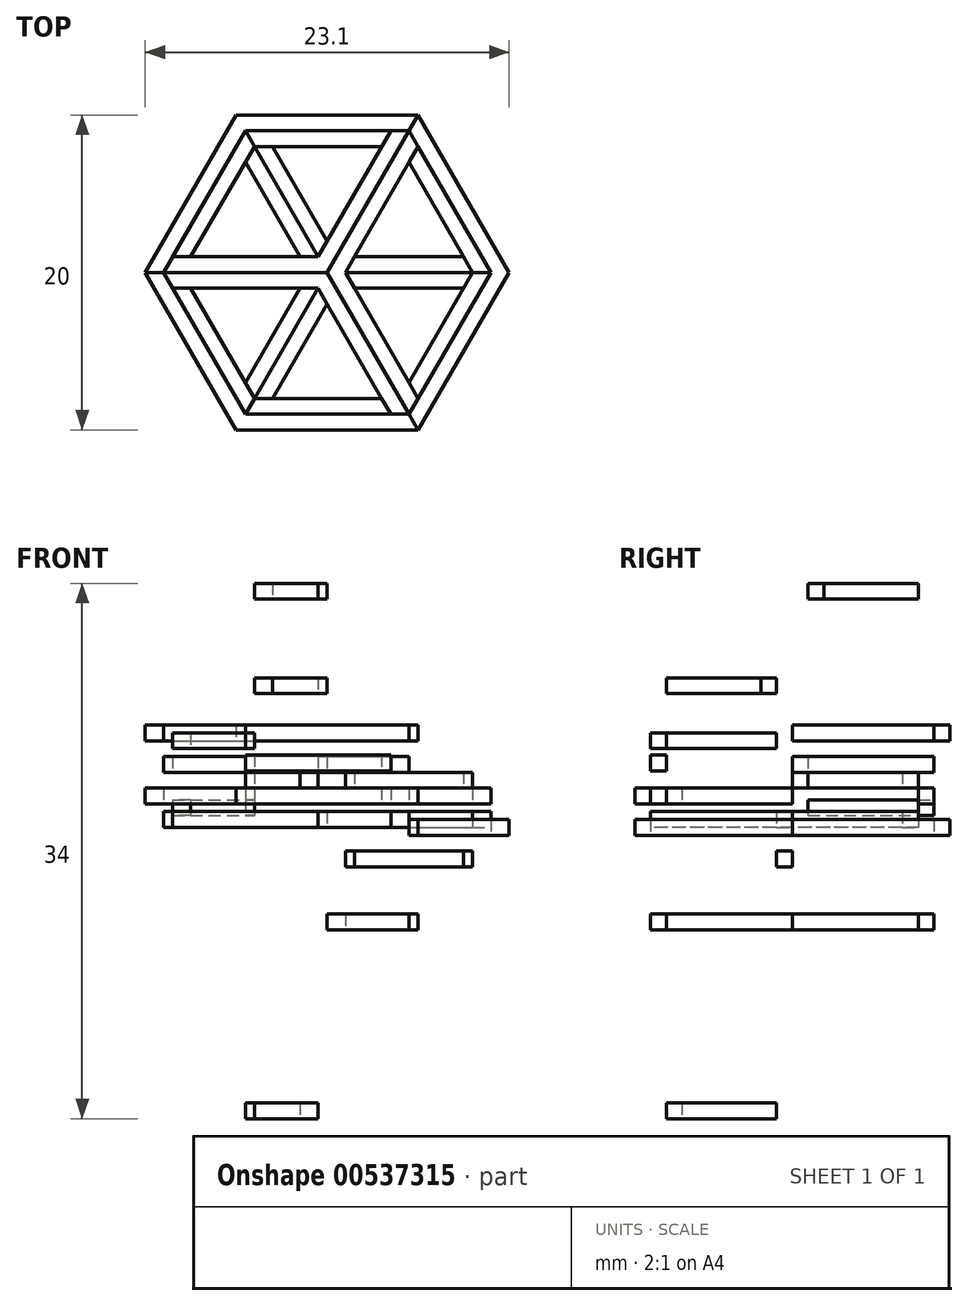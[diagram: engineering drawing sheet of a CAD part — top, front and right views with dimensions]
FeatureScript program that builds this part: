
annotation { "Feature Type Name" : "Feature", "Feature Type Description" : "" }
export const myFeature = defineFeature(function(context is Context, id is Id, definition is map)
    precondition{}
    {
        {
            var Q0;
            Q0=qCreatedBy(makeId("Top.planeOp"),FACE);
            var sketch = newSketch(context, id + "F0", { "sketchPlane" : qUnion([Q0])});
            skLineSegment(sketch, "E0", {"start": v(0, 0) * mm, "end": v(0, 10) * mm});
            skArc(sketch, "E1.cCircle", {"start": v(4.36, 9) * mm, "mid": v(-5, -8.66) * mm, "end": v(5.61, 8.27) * mm, "construction": true});
            skLineSegment(sketch, "E1.0", {"start": v(-5.77, 10) * mm, "end": v(5.77, 10) * mm});
            skLineSegment(sketch, "E1.1", {"start": v(5.77, 10) * mm, "end": v(11.55, 0) * mm});
            skLineSegment(sketch, "E1.2", {"start": v(11.55, 0) * mm, "end": v(5.77, -10) * mm});
            skLineSegment(sketch, "E1.3", {"start": v(5.77, -10) * mm, "end": v(-5.77, -10) * mm});
            skLineSegment(sketch, "E1.4", {"start": v(-5.77, -10) * mm, "end": v(-11.55, 0) * mm});
            skLineSegment(sketch, "E1.5", {"start": v(-11.55, 0) * mm, "end": v(-5.77, 10) * mm});
            skPoint(sketch, "E1.0.midPoint", {"position": v(0, 10) * mm});
            skLineSegment(sketch, "E2.0", {"start": v(-10.4, 0) * mm, "end": v(-5.2, 9) * mm});
            skLineSegment(sketch, "E2.1", {"start": v(5.2, 9) * mm, "end": v(10.4, 0) * mm});
            skLineSegment(sketch, "E2.2", {"start": v(10.4, 0) * mm, "end": v(5.2, -9) * mm});
            skLineSegment(sketch, "E2.3", {"start": v(-5.2, 9) * mm, "end": v(5.2, 9) * mm});
            skLineSegment(sketch, "E2.4", {"start": v(5.2, -9) * mm, "end": v(-5.2, -9) * mm});
            skLineSegment(sketch, "E2.5", {"start": v(-5.2, -9) * mm, "end": v(-10.4, 0) * mm});
            skLineSegment(sketch, "E3.0", {"start": v(-9.24, 0) * mm, "end": v(-4.62, 8) * mm});
            skLineSegment(sketch, "E3.1", {"start": v(4.62, 8) * mm, "end": v(9.24, 0) * mm});
            skLineSegment(sketch, "E3.2", {"start": v(9.24, 0) * mm, "end": v(4.62, -8) * mm});
            skLineSegment(sketch, "E3.3", {"start": v(-4.62, 8) * mm, "end": v(4.62, 8) * mm});
            skLineSegment(sketch, "E3.4", {"start": v(4.62, -8) * mm, "end": v(-4.62, -8) * mm});
            skLineSegment(sketch, "E3.5", {"start": v(-4.62, -8) * mm, "end": v(-9.24, 0) * mm});
            skLineSegment(sketch, "E4", {"start": v(0, 0) * mm, "end": v(4.62, -8) * mm});
            skLineSegment(sketch, "E5", {"start": v(0, 0) * mm, "end": v(4.62, 8) * mm});
            skLineSegment(sketch, "E6", {"start": v(0, 0) * mm, "end": v(-9.24, 0) * mm});
            skLineSegment(sketch, "E7.0", {"start": v(-0.58, 1) * mm, "end": v(3.46, 8) * mm});
            skLineSegment(sketch, "E7.1", {"start": v(-0.58, 1) * mm, "end": v(-9.81, 1) * mm});
            skLineSegment(sketch, "E8.0", {"start": v(1.15, 0) * mm, "end": v(5.77, 8) * mm});
            skLineSegment(sketch, "E9.0", {"start": v(-0.58, -1) * mm, "end": v(4.04, -9) * mm});
            skLineSegment(sketch, "E10.0", {"start": v(1.15, 0) * mm, "end": v(5.77, -8) * mm});
            skLineSegment(sketch, "E11.0", {"start": v(-0.58, -1) * mm, "end": v(-9.81, -1) * mm});
            skLineSegment(sketch, "E12.1.0", {"start": v(0.58, -1) * mm, "end": v(-3.46, -8) * mm});
            skLineSegment(sketch, "E12.1.1", {"start": v(-1.15, 0) * mm, "end": v(-5.2, -7) * mm});
            skLineSegment(sketch, "E12.1.2", {"start": v(-1.15, 0) * mm, "end": v(-5.2, 7) * mm});
            skLineSegment(sketch, "E12.1.3", {"start": v(0.58, 1) * mm, "end": v(-3.46, 8) * mm});
            skLineSegment(sketch, "E12.1.4", {"start": v(0, 0) * mm, "end": v(-4.62, 8) * mm});
            skLineSegment(sketch, "E12.1.5", {"start": v(0.58, 1) * mm, "end": v(8.66, 1) * mm});
            skLineSegment(sketch, "E12.1.6", {"start": v(0.58, -1) * mm, "end": v(8.66, -1) * mm});
            skLineSegment(sketch, "E12.1.7", {"start": v(0, 0) * mm, "end": v(9.24, 0) * mm});
            skLineSegment(sketch, "E12.1.8", {"start": v(0, 0) * mm, "end": v(-4.62, -8) * mm});
            skLineSegment(sketch, "E13", {"start": v(-4.62, 8) * mm, "end": v(-5.2, 9) * mm});
            skLineSegment(sketch, "E14", {"start": v(3.46, 8) * mm, "end": v(4.04, 9) * mm});
            skPoint(sketch, "E15.orphan", {"position": v(5.2, 7) * mm});
            skPoint(sketch, "E16.orphan", {"position": v(5.2, -7) * mm});
            skPoint(sketch, "E17.orphan", {"position": v(3.46, -8) * mm});
            skPoint(sketch, "E18.orphan", {"position": v(-8.66, -1) * mm});
            skPoint(sketch, "E19.orphan", {"position": v(-8.66, 1) * mm});
            skLineSegment(sketch, "E20", {"start": v(5.2, 9) * mm, "end": v(5.77, 10) * mm});
            skLineSegment(sketch, "E21", {"start": v(-10.4, 0) * mm, "end": v(-11.55, 0) * mm});
            skLineSegment(sketch, "E22", {"start": v(5.2, -9) * mm, "end": v(5.77, -10) * mm});
            skLineSegment(sketch, "E23", {"start": v(9.24, 0) * mm, "end": v(10.4, 0) * mm});
            skLineSegment(sketch, "E24", {"start": v(-4.62, -8) * mm, "end": v(-5.2, -9) * mm});
            skLineSegment(sketch, "E25", {"start": v(4.62, 8) * mm, "end": v(5.2, 9) * mm});
            skLineSegment(sketch, "E26", {"start": v(-9.24, 0) * mm, "end": v(-10.4, 0) * mm});
            skLineSegment(sketch, "E27", {"start": v(4.62, -8) * mm, "end": v(5.2, -9) * mm});
            skSolve(sketch);
        }
        {
            var Q0;
            {var subQ3=sQuery(id+"F0.wireOp",EDGE,"E1.5");Q0=makeQuery(id+"F0.imprint","IMPRINT",FACE,{"disambiguationData":[TD([[makeQuery(id+"F0.imprint","IMPRINT",EDGE,{"derivedFrom":subQ3}),-1.0]])]});}
            var Q1;
            {var subQ0=sQuery(id+"F0.wireOp",EDGE,"E20");Q1=makeQuery(id+"F0.imprint","IMPRINT",FACE,{"disambiguationData":[TD([[makeQuery(id+"F0.imprint","IMPRINT",EDGE,{"derivedFrom":subQ0}),1.0]])]});}
            extrude(context, id + "F1", {"entities" : qUnion([Q0, Q1]), "depth" : 1 * mm, "offsetDistance" : 25 * mm});
        }
        {
            var Q0;
            {var subQ1=sQuery(id+"F0.wireOp",EDGE,"E3.0");var subQ3=sQuery(id+"F0.wireOp",EDGE,"E7.1");var subQ4=makeQuery(id+"F0.imprint","INTERSECT",VERTEX,{"derivedFrom":[subQ1,subQ3]});Q0=makeQuery(id+"F0.imprint","IMPRINT",FACE,{"disambiguationData":[TD([[makeQuery(id+"F0.imprint","IMPRINT",EDGE,{"disambiguationData":[TD([[subQ4,1.0]])],"derivedFrom":subQ3}),1.0]])]});}
            var Q1;
            {var subQ3=sQuery(id+"F0.wireOp",EDGE,"E12.1.2");var subQ5=sQuery(id+"F0.wireOp",EDGE,"E7.1");var subQ7=makeQuery(id+"F0.imprint","INTERSECT",VERTEX,{"derivedFrom":[subQ5,subQ3]});Q1=makeQuery(id+"F0.imprint","IMPRINT",FACE,{"disambiguationData":[TD([[makeQuery(id+"F0.imprint","IMPRINT",EDGE,{"disambiguationData":[TD([[subQ7,1.0]])],"derivedFrom":subQ5}),1.0]])]});}
            var Q2;
            {var subQ0=sQuery(id+"F0.wireOp",EDGE,"E12.1.4");var subQ3=sQuery(id+"F0.wireOp",EDGE,"E7.0");var subQ5=makeQuery(id+"F0.imprint","INTERSECT",VERTEX,{"derivedFrom":[subQ3,sQuery(id+"F0.wireOp",EDGE,"E7.1"),subQ0]});Q2=makeQuery(id+"F0.imprint","IMPRINT",FACE,{"disambiguationData":[TD([[makeQuery(id+"F0.imprint","IMPRINT",EDGE,{"disambiguationData":[TD([[subQ5,-1.0]])],"derivedFrom":subQ3}),-1.0]])]});}
            var Q3;
            {var subQ0=sQuery(id+"F0.wireOp",EDGE,"E5");var subQ3=sQuery(id+"F0.wireOp",EDGE,"E12.1.3");var subQ5=makeQuery(id+"F0.imprint","INTERSECT",VERTEX,{"derivedFrom":[subQ0,subQ3,sQuery(id+"F0.wireOp",EDGE,"E12.1.5")]});Q3=makeQuery(id+"F0.imprint","IMPRINT",FACE,{"disambiguationData":[TD([[makeQuery(id+"F0.imprint","IMPRINT",EDGE,{"disambiguationData":[TD([[subQ5,-1.0]])],"derivedFrom":subQ3}),1.0]])]});}
            var Q4;
            {var subQ0=sQuery(id+"F0.wireOp",EDGE,"E5");var subQ1=sQuery(id+"F0.wireOp",EDGE,"E3.3");var subQ2=makeQuery(id+"F0.imprint","INTERSECT",VERTEX,{"derivedFrom":[sQuery(id+"F0.wireOp",EDGE,"E3.1"),subQ1,subQ0]});Q4=makeQuery(id+"F0.imprint","IMPRINT",FACE,{"disambiguationData":[TD([[makeQuery(id+"F0.imprint","IMPRINT",EDGE,{"disambiguationData":[TD([[subQ2,1.0]])],"derivedFrom":subQ1}),-1.0]])]});}
            var Q5;
            {var subQ0=sQuery(id+"F0.wireOp",EDGE,"E26");Q5=makeQuery(id+"F0.imprint","IMPRINT",FACE,{"disambiguationData":[TD([[makeQuery(id+"F0.imprint","IMPRINT",EDGE,{"derivedFrom":subQ0}),-1.0]])]});}
            var Q6;
            {var subQ2=sQuery(id+"F0.wireOp",EDGE,"E14");Q6=makeQuery(id+"F0.imprint","IMPRINT",FACE,{"disambiguationData":[TD([[makeQuery(id+"F0.imprint","IMPRINT",EDGE,{"derivedFrom":subQ2}),-1.0]])]});}
            extrude(context, id + "F2", {"entities" : qUnion([Q0, Q1, Q2, Q3, Q4, Q5, Q6]), "depth" : 1 * mm, "offsetDistance" : 25 * mm});
        }
        {
            var Q0;
            {var subQ5=sQuery(id+"F0.wireOp",EDGE,"E24");Q0=makeQuery(id+"F0.imprint","IMPRINT",FACE,{"disambiguationData":[TD([[makeQuery(id+"F0.imprint","IMPRINT",EDGE,{"derivedFrom":subQ5}),1.0]])]});}
            var Q1;
            {var subQ6=sQuery(id+"F0.wireOp",EDGE,"E23");Q1=makeQuery(id+"F0.imprint","IMPRINT",FACE,{"disambiguationData":[TD([[makeQuery(id+"F0.imprint","IMPRINT",EDGE,{"derivedFrom":subQ6}),-1.0]])]});}
            var Q2;
            {var subQ1=sQuery(id+"F0.wireOp",EDGE,"E3.1");var subQ3=sQuery(id+"F0.wireOp",EDGE,"E12.1.5");var subQ4=makeQuery(id+"F0.imprint","INTERSECT",VERTEX,{"derivedFrom":[subQ1,subQ3]});Q2=makeQuery(id+"F0.imprint","IMPRINT",FACE,{"disambiguationData":[TD([[makeQuery(id+"F0.imprint","IMPRINT",EDGE,{"disambiguationData":[TD([[subQ4,1.0]])],"derivedFrom":subQ3}),-1.0]])]});}
            var Q3;
            {var subQ1=sQuery(id+"F0.wireOp",EDGE,"E3.5");var subQ3=sQuery(id+"F0.wireOp",EDGE,"E12.1.1");var subQ4=makeQuery(id+"F0.imprint","INTERSECT",VERTEX,{"derivedFrom":[subQ1,subQ3]});Q3=makeQuery(id+"F0.imprint","IMPRINT",FACE,{"disambiguationData":[TD([[makeQuery(id+"F0.imprint","IMPRINT",EDGE,{"disambiguationData":[TD([[subQ4,1.0]])],"derivedFrom":subQ3}),1.0]])]});}
            extrude(context, id + "F3", {"entities" : qUnion([Q0, Q1, Q2, Q3]), "depth" : 1 * mm, "offsetDistance" : 25 * mm});
        }
        {
            var Q0;
            Q0=makeQuery(id+"F0.imprint","IMPRINT",FACE,{"disambiguationData":[TD([[makeQuery(id+"F0.imprint","IMPRINT",EDGE,{"derivedFrom":sQuery(id+"F0.wireOp",EDGE,"E1.3")}),-1.0]])]});
            var Q1;
            {var subQ5=sQuery(id+"F0.wireOp",EDGE,"E23");Q1=makeQuery(id+"F0.imprint","IMPRINT",FACE,{"disambiguationData":[TD([[makeQuery(id+"F0.imprint","IMPRINT",EDGE,{"derivedFrom":subQ5}),1.0]])]});}
            var Q2;
            {var subQ5=sQuery(id+"F0.wireOp",EDGE,"E14");Q2=makeQuery(id+"F0.imprint","IMPRINT",FACE,{"disambiguationData":[TD([[makeQuery(id+"F0.imprint","IMPRINT",EDGE,{"derivedFrom":subQ5}),1.0]])]});}
            var Q3;
            {var subQ4=sQuery(id+"F0.wireOp",EDGE,"E13");Q3=makeQuery(id+"F0.imprint","IMPRINT",FACE,{"disambiguationData":[TD([[makeQuery(id+"F0.imprint","IMPRINT",EDGE,{"derivedFrom":subQ4}),-1.0]])]});}
            extrude(context, id + "F4", {"entities" : qUnion([Q0, Q1, Q2, Q3]), "depth" : 1 * mm, "offsetDistance" : 25 * mm});
        }
        {
            var Q0;
            {var subQ0=sQuery(id+"F0.wireOp",EDGE,"E26");Q0=makeQuery(id+"F0.imprint","IMPRINT",FACE,{"disambiguationData":[TD([[makeQuery(id+"F0.imprint","IMPRINT",EDGE,{"derivedFrom":subQ0}),1.0]])]});}
            var Q1;
            {var subQ1=sQuery(id+"F0.wireOp",EDGE,"E3.5");var subQ3=sQuery(id+"F0.wireOp",EDGE,"E11.0");var subQ4=makeQuery(id+"F0.imprint","INTERSECT",VERTEX,{"derivedFrom":[subQ1,subQ3]});Q1=makeQuery(id+"F0.imprint","IMPRINT",FACE,{"disambiguationData":[TD([[makeQuery(id+"F0.imprint","IMPRINT",EDGE,{"disambiguationData":[TD([[subQ4,1.0]])],"derivedFrom":subQ3}),-1.0]])]});}
            var Q2;
            {var subQ3=sQuery(id+"F0.wireOp",EDGE,"E12.1.1");var subQ5=sQuery(id+"F0.wireOp",EDGE,"E11.0");var subQ7=makeQuery(id+"F0.imprint","INTERSECT",VERTEX,{"derivedFrom":[subQ5,subQ3]});Q2=makeQuery(id+"F0.imprint","IMPRINT",FACE,{"disambiguationData":[TD([[makeQuery(id+"F0.imprint","IMPRINT",EDGE,{"disambiguationData":[TD([[subQ7,1.0]])],"derivedFrom":subQ5}),-1.0]])]});}
            var Q3;
            {var subQ3=sQuery(id+"F0.wireOp",EDGE,"E12.1.0");var subQ5=sQuery(id+"F0.wireOp",EDGE,"E9.0");var subQ7=makeQuery(id+"F0.imprint","INTERSECT",VERTEX,{"derivedFrom":[subQ5,subQ3]});Q3=makeQuery(id+"F0.imprint","IMPRINT",FACE,{"disambiguationData":[TD([[makeQuery(id+"F0.imprint","IMPRINT",EDGE,{"disambiguationData":[TD([[subQ7,1.0]])],"derivedFrom":subQ5}),1.0]])]});}
            var Q4;
            {var subQ1=sQuery(id+"F0.wireOp",EDGE,"E3.4");var subQ3=sQuery(id+"F0.wireOp",EDGE,"E9.0");var subQ4=makeQuery(id+"F0.imprint","INTERSECT",VERTEX,{"derivedFrom":[subQ1,subQ3]});Q4=makeQuery(id+"F0.imprint","IMPRINT",FACE,{"disambiguationData":[TD([[makeQuery(id+"F0.imprint","IMPRINT",EDGE,{"disambiguationData":[TD([[subQ4,1.0]])],"derivedFrom":subQ3}),1.0]])]});}
            var Q5;
            {var subQ0=sQuery(id+"F0.wireOp",EDGE,"E27");Q5=makeQuery(id+"F0.imprint","IMPRINT",FACE,{"disambiguationData":[TD([[makeQuery(id+"F0.imprint","IMPRINT",EDGE,{"derivedFrom":subQ0}),-1.0]])]});}
            extrude(context, id + "F5", {"entities" : qUnion([Q0, Q1, Q2, Q3, Q4, Q5]), "depth" : 1 * mm, "offsetDistance" : 25 * mm});
        }
        {
            var Q0;
            {var subQ5=sQuery(id+"F0.wireOp",EDGE,"E13");Q0=makeQuery(id+"F0.imprint","IMPRINT",FACE,{"disambiguationData":[TD([[makeQuery(id+"F0.imprint","IMPRINT",EDGE,{"derivedFrom":subQ5}),1.0]])]});}
            var Q1;
            {var subQ6=sQuery(id+"F0.wireOp",EDGE,"E24");Q1=makeQuery(id+"F0.imprint","IMPRINT",FACE,{"disambiguationData":[TD([[makeQuery(id+"F0.imprint","IMPRINT",EDGE,{"derivedFrom":subQ6}),-1.0]])]});}
            var Q2;
            {var subQ0=sQuery(id+"F0.wireOp",EDGE,"E27");Q2=makeQuery(id+"F0.imprint","IMPRINT",FACE,{"disambiguationData":[TD([[makeQuery(id+"F0.imprint","IMPRINT",EDGE,{"derivedFrom":subQ0}),1.0]])]});}
            var Q3;
            {var subQ1=sQuery(id+"F0.wireOp",EDGE,"E3.2");var subQ3=sQuery(id+"F0.wireOp",EDGE,"E10.0");var subQ4=makeQuery(id+"F0.imprint","INTERSECT",VERTEX,{"derivedFrom":[subQ1,subQ3]});Q3=makeQuery(id+"F0.imprint","IMPRINT",FACE,{"disambiguationData":[TD([[makeQuery(id+"F0.imprint","IMPRINT",EDGE,{"disambiguationData":[TD([[subQ4,1.0]])],"derivedFrom":subQ3}),-1.0]])]});}
            var Q4;
            {var subQ3=sQuery(id+"F0.wireOp",EDGE,"E12.1.5");var subQ5=sQuery(id+"F0.wireOp",EDGE,"E8.0");var subQ7=makeQuery(id+"F0.imprint","INTERSECT",VERTEX,{"derivedFrom":[subQ5,subQ3]});Q4=makeQuery(id+"F0.imprint","IMPRINT",FACE,{"disambiguationData":[TD([[makeQuery(id+"F0.imprint","IMPRINT",EDGE,{"disambiguationData":[TD([[subQ7,1.0]])],"derivedFrom":subQ5}),1.0]])]});}
            var Q5;
            {var subQ3=sQuery(id+"F0.wireOp",EDGE,"E12.1.6");var subQ5=sQuery(id+"F0.wireOp",EDGE,"E10.0");var subQ6=makeQuery(id+"F0.imprint","INTERSECT",VERTEX,{"derivedFrom":[subQ5,subQ3]});Q5=makeQuery(id+"F0.imprint","IMPRINT",FACE,{"disambiguationData":[TD([[makeQuery(id+"F0.imprint","IMPRINT",EDGE,{"disambiguationData":[TD([[subQ6,1.0]])],"derivedFrom":subQ5}),-1.0]])]});}
            var Q6;
            {var subQ1=sQuery(id+"F0.wireOp",EDGE,"E3.1");var subQ3=sQuery(id+"F0.wireOp",EDGE,"E8.0");var subQ4=makeQuery(id+"F0.imprint","INTERSECT",VERTEX,{"derivedFrom":[subQ1,subQ3]});Q6=makeQuery(id+"F0.imprint","IMPRINT",FACE,{"disambiguationData":[TD([[makeQuery(id+"F0.imprint","IMPRINT",EDGE,{"disambiguationData":[TD([[subQ4,1.0]])],"derivedFrom":subQ3}),1.0]])]});}
            var Q7;
            {var subQ0=sQuery(id+"F0.wireOp",EDGE,"E25");Q7=makeQuery(id+"F0.imprint","IMPRINT",FACE,{"disambiguationData":[TD([[makeQuery(id+"F0.imprint","IMPRINT",EDGE,{"derivedFrom":subQ0}),-1.0]])]});}
            extrude(context, id + "F6", {"entities" : qUnion([Q0, Q1, Q2, Q3, Q4, Q5, Q6, Q7]), "depth" : 1 * mm, "offsetDistance" : 25 * mm});
        }
        {
            var Q0;
            Q0=makeQuery(id+"F0.imprint","IMPRINT",FACE,{"disambiguationData":[TD([[makeQuery(id+"F0.imprint","IMPRINT",EDGE,{"derivedFrom":sQuery(id+"F0.wireOp",EDGE,"E1.1")}),-1.0]])]});
            var Q1;
            {var subQ1=sQuery(id+"F0.wireOp",EDGE,"E3.3");var subQ3=sQuery(id+"F0.wireOp",EDGE,"E12.1.3");var subQ4=makeQuery(id+"F0.imprint","INTERSECT",VERTEX,{"derivedFrom":[subQ1,subQ3]});Q1=makeQuery(id+"F0.imprint","IMPRINT",FACE,{"disambiguationData":[TD([[makeQuery(id+"F0.imprint","IMPRINT",EDGE,{"disambiguationData":[TD([[subQ4,1.0]])],"derivedFrom":subQ3}),1.0]])]});}
            extrude(context, id + "F7", {"entities" : qUnion([Q0, Q1]), "depth" : 1 * mm, "offsetDistance" : 25 * mm});
        }
        {
            var Q0;
            {var subQ1=sQuery(id+"F0.wireOp",EDGE,"E3.0");var subQ3=sQuery(id+"F0.wireOp",EDGE,"E12.1.2");var subQ4=makeQuery(id+"F0.imprint","INTERSECT",VERTEX,{"derivedFrom":[subQ1,subQ3]});Q0=makeQuery(id+"F0.imprint","IMPRINT",FACE,{"disambiguationData":[TD([[makeQuery(id+"F0.imprint","IMPRINT",EDGE,{"disambiguationData":[TD([[subQ4,1.0]])],"derivedFrom":subQ3}),-1.0]])]});}
            var Q1;
            {var subQ1=sQuery(id+"F0.wireOp",EDGE,"E3.4");var subQ3=sQuery(id+"F0.wireOp",EDGE,"E12.1.0");var subQ4=makeQuery(id+"F0.imprint","INTERSECT",VERTEX,{"derivedFrom":[subQ1,subQ3]});Q1=makeQuery(id+"F0.imprint","IMPRINT",FACE,{"disambiguationData":[TD([[makeQuery(id+"F0.imprint","IMPRINT",EDGE,{"disambiguationData":[TD([[subQ4,1.0]])],"derivedFrom":subQ3}),-1.0]])]});}
            var Q2;
            {var subQ1=sQuery(id+"F0.wireOp",EDGE,"E3.2");var subQ3=sQuery(id+"F0.wireOp",EDGE,"E12.1.6");var subQ4=makeQuery(id+"F0.imprint","INTERSECT",VERTEX,{"derivedFrom":[subQ1,subQ3]});Q2=makeQuery(id+"F0.imprint","IMPRINT",FACE,{"disambiguationData":[TD([[makeQuery(id+"F0.imprint","IMPRINT",EDGE,{"disambiguationData":[TD([[subQ4,1.0]])],"derivedFrom":subQ3}),1.0]])]});}
            extrude(context, id + "F8", {"entities" : qUnion([Q0, Q1, Q2]), "depth" : 1 * mm, "offsetDistance" : 25 * mm});
        }
        {
            var Q0;
            Q0=makeQuery(id+"F1.opExtrude","SWEPT_BODY",BODY,{"disambiguationData":[OSD([sQuery(id+"F0.wireOp",EDGE,"E1.0"),sQuery(id+"F0.wireOp",EDGE,"E1.5"),sQuery(id+"F0.wireOp",EDGE,"E2.0"),sQuery(id+"F0.wireOp",EDGE,"E2.3"),sQuery(id+"F0.wireOp",EDGE,"E20"),sQuery(id+"F0.wireOp",EDGE,"E21")])]});
            transform(context, id + "F9", {"entities" : qUnion([Q0]), "transformType" : TransformType.TRANSLATION_3D, "dx" : 0 * mm, "dy" : 0 * mm, "dz" : 4 * mm, "makeCopy" : false});
        }
        {
            var Q0;
            Q0=makeQuery(id+"F7.opExtrude","SWEPT_BODY",BODY,{"disambiguationData":[OSD([sQuery(id+"F0.wireOp",EDGE,"E3.3"),sQuery(id+"F0.wireOp",EDGE,"E7.0"),sQuery(id+"F0.wireOp",EDGE,"E12.1.3"),sQuery(id+"F0.wireOp",EDGE,"E12.1.4")])]});
            transform(context, id + "F10", {"entities" : qUnion([Q0]), "transformType" : TransformType.TRANSLATION_3D, "dx" : 0 * mm, "dy" : 0 * mm, "dz" : 3 * mm, "makeCopy" : false});
        }
        {
            var Q0;
            Q0=makeQuery(id+"F2.opExtrude","SWEPT_BODY",BODY,{"disambiguationData":[OSD([sQuery(id+"F0.wireOp",EDGE,"E2.0"),sQuery(id+"F0.wireOp",EDGE,"E2.3"),sQuery(id+"F0.wireOp",EDGE,"E5"),sQuery(id+"F0.wireOp",EDGE,"E6"),sQuery(id+"F0.wireOp",EDGE,"E7.0"),sQuery(id+"F0.wireOp",EDGE,"E7.1"),sQuery(id+"F0.wireOp",EDGE,"E14"),sQuery(id+"F0.wireOp",EDGE,"E25"),sQuery(id+"F0.wireOp",EDGE,"E26")])]});
            transform(context, id + "F11", {"entities" : qUnion([Q0]), "transformType" : TransformType.TRANSLATION_3D, "dx" : 0 * mm, "dy" : 0 * mm, "dz" : 2 * mm, "makeCopy" : false});
        }
        {
            var Q0;
            Q0=makeQuery(id+"F8.opExtrude","SWEPT_BODY",BODY,{"disambiguationData":[OSD([sQuery(id+"F0.wireOp",EDGE,"E3.0"),sQuery(id+"F0.wireOp",EDGE,"E7.1"),sQuery(id+"F0.wireOp",EDGE,"E12.1.2"),sQuery(id+"F0.wireOp",EDGE,"E12.1.4")])]});
            transform(context, id + "F12", {"entities" : qUnion([Q0]), "transformType" : TransformType.TRANSLATION_3D, "dx" : 0 * mm, "dy" : 0 * mm, "dz" : 1 * mm, "makeCopy" : false});
        }
        {
            var Q0;
            Q0=makeQuery(id+"F6.opExtrude","SWEPT_BODY",BODY,{"disambiguationData":[OSD([sQuery(id+"F0.wireOp",EDGE,"E2.0"),sQuery(id+"F0.wireOp",EDGE,"E3.0"),sQuery(id+"F0.wireOp",EDGE,"E7.1"),sQuery(id+"F0.wireOp",EDGE,"E13")])]});
            transform(context, id + "F13", {"entities" : qUnion([Q0]), "transformType" : TransformType.TRANSLATION_3D, "dx" : 0 * mm, "dy" : 0 * mm, "dz" : -0.75 * mm, "makeCopy" : false});
        }
        {
            var Q0;
            Q0=makeQuery(id+"F7.opExtrude","SWEPT_BODY",BODY,{"disambiguationData":[OSD([sQuery(id+"F0.wireOp",EDGE,"E1.1"),sQuery(id+"F0.wireOp",EDGE,"E1.2"),sQuery(id+"F0.wireOp",EDGE,"E2.1"),sQuery(id+"F0.wireOp",EDGE,"E2.2"),sQuery(id+"F0.wireOp",EDGE,"E20"),sQuery(id+"F0.wireOp",EDGE,"E22")])]});
            transform(context, id + "F14", {"entities" : qUnion([Q0]), "transformType" : TransformType.TRANSLATION_3D, "dx" : 0 * mm, "dy" : 0 * mm, "dz" : -2 * mm, "makeCopy" : false});
        }
        {
            var Q0;
            Q0=makeQuery(id+"F5.opExtrude","SWEPT_BODY",BODY,{"disambiguationData":[OSD([sQuery(id+"F0.wireOp",EDGE,"E2.4"),sQuery(id+"F0.wireOp",EDGE,"E2.5"),sQuery(id+"F0.wireOp",EDGE,"E4"),sQuery(id+"F0.wireOp",EDGE,"E6"),sQuery(id+"F0.wireOp",EDGE,"E9.0"),sQuery(id+"F0.wireOp",EDGE,"E11.0"),sQuery(id+"F0.wireOp",EDGE,"E26"),sQuery(id+"F0.wireOp",EDGE,"E27")])]});
            transform(context, id + "F15", {"entities" : qUnion([Q0]), "transformType" : TransformType.TRANSLATION_3D, "dx" : 0 * mm, "dy" : 0 * mm, "dz" : -1 * mm, "makeCopy" : false});
        }
        {
            var Q0;
            Q0=makeQuery(id+"F8.opExtrude","SWEPT_BODY",BODY,{"disambiguationData":[OSD([sQuery(id+"F0.wireOp",EDGE,"E3.2"),sQuery(id+"F0.wireOp",EDGE,"E10.0"),sQuery(id+"F0.wireOp",EDGE,"E12.1.6"),sQuery(id+"F0.wireOp",EDGE,"E12.1.7")])]});
            transform(context, id + "F16", {"entities" : qUnion([Q0]), "transformType" : TransformType.TRANSLATION_3D, "dx" : 0 * mm, "dy" : 0 * mm, "dz" : -4 * mm, "makeCopy" : false});
        }
        {
            var Q0;
            Q0=makeQuery(id+"F8.opExtrude","SWEPT_BODY",BODY,{"disambiguationData":[OSD([sQuery(id+"F0.wireOp",EDGE,"E3.4"),sQuery(id+"F0.wireOp",EDGE,"E9.0"),sQuery(id+"F0.wireOp",EDGE,"E12.1.0"),sQuery(id+"F0.wireOp",EDGE,"E12.1.8")])]});
            transform(context, id + "F17", {"entities" : qUnion([Q0]), "transformType" : TransformType.TRANSLATION_3D, "dx" : 0 * mm, "dy" : 0 * mm, "dz" : 7 * mm, "makeCopy" : false});
        }
        {
            var Q0;
            Q0=makeQuery(id+"F6.opExtrude","SWEPT_BODY",BODY,{"disambiguationData":[OSD([sQuery(id+"F0.wireOp",EDGE,"E2.1"),sQuery(id+"F0.wireOp",EDGE,"E2.2"),sQuery(id+"F0.wireOp",EDGE,"E4"),sQuery(id+"F0.wireOp",EDGE,"E5"),sQuery(id+"F0.wireOp",EDGE,"E8.0"),sQuery(id+"F0.wireOp",EDGE,"E10.0"),sQuery(id+"F0.wireOp",EDGE,"E25"),sQuery(id+"F0.wireOp",EDGE,"E27")])]});
            transform(context, id + "F18", {"entities" : qUnion([Q0]), "transformType" : TransformType.TRANSLATION_3D, "dx" : 0 * mm, "dy" : 0 * mm, "dz" : -8 * mm, "makeCopy" : false});
        }
        {
            var Q0;
            Q0=makeQuery(id+"F6.opExtrude","SWEPT_BODY",BODY,{"disambiguationData":[OSD([sQuery(id+"F0.wireOp",EDGE,"E2.5"),sQuery(id+"F0.wireOp",EDGE,"E3.5"),sQuery(id+"F0.wireOp",EDGE,"E11.0"),sQuery(id+"F0.wireOp",EDGE,"E24")])]});
            transform(context, id + "F19", {"entities" : qUnion([Q0]), "transformType" : TransformType.TRANSLATION_3D, "dx" : 0 * mm, "dy" : 0 * mm, "dz" : 3.5 * mm, "makeCopy" : false});
        }
        {
            var Q0;
            Q0=makeQuery(id+"F3.opExtrude","SWEPT_BODY",BODY,{"disambiguationData":[OSD([sQuery(id+"F0.wireOp",EDGE,"E3.1"),sQuery(id+"F0.wireOp",EDGE,"E8.0"),sQuery(id+"F0.wireOp",EDGE,"E12.1.5"),sQuery(id+"F0.wireOp",EDGE,"E12.1.7")])]});
            transform(context, id + "F20", {"entities" : qUnion([Q0]), "transformType" : TransformType.TRANSLATION_3D, "dx" : 0 * mm, "dy" : 0 * mm, "dz" : 1 * mm, "makeCopy" : false});
        }
        {
            var Q0;
            Q0=makeQuery(id+"F4.opExtrude","SWEPT_BODY",BODY,{"disambiguationData":[OSD([sQuery(id+"F0.wireOp",EDGE,"E2.1"),sQuery(id+"F0.wireOp",EDGE,"E3.1"),sQuery(id+"F0.wireOp",EDGE,"E8.0"),sQuery(id+"F0.wireOp",EDGE,"E23")])]});
            transform(context, id + "F21", {"entities" : qUnion([Q0]), "transformType" : TransformType.TRANSLATION_3D, "dx" : 0 * mm, "dy" : 0 * mm, "dz" : -1.5 * mm, "makeCopy" : false});
        }
        {
            var Q0;
            Q0=makeQuery(id+"F3.opExtrude","SWEPT_BODY",BODY,{"disambiguationData":[OSD([sQuery(id+"F0.wireOp",EDGE,"E3.5"),sQuery(id+"F0.wireOp",EDGE,"E11.0"),sQuery(id+"F0.wireOp",EDGE,"E12.1.1"),sQuery(id+"F0.wireOp",EDGE,"E12.1.8")])]});
            transform(context, id + "F22", {"entities" : qUnion([Q0]), "transformType" : TransformType.TRANSLATION_3D, "dx" : 0 * mm, "dy" : 0 * mm, "dz" : -20 * mm, "makeCopy" : false});
        }
        {
            var Q0;
            Q0=makeQuery(id+"F7.opExtrude","SWEPT_BODY",BODY,{"disambiguationData":[OSD([sQuery(id+"F0.wireOp",EDGE,"E3.3"),sQuery(id+"F0.wireOp",EDGE,"E7.0"),sQuery(id+"F0.wireOp",EDGE,"E12.1.3"),sQuery(id+"F0.wireOp",EDGE,"E12.1.4")])]});
            transform(context, id + "F23", {"entities" : qUnion([Q0]), "transformType" : TransformType.TRANSLATION_3D, "dx" : 0 * mm, "dy" : 0 * mm, "dz" : 10 * mm, "makeCopy" : false});
        }
        {
            var Q0;
            Q0=makeQuery(id+"F3.opExtrude","SWEPT_BODY",BODY,{"disambiguationData":[OSD([sQuery(id+"F0.wireOp",EDGE,"E2.4"),sQuery(id+"F0.wireOp",EDGE,"E3.4"),sQuery(id+"F0.wireOp",EDGE,"E9.0"),sQuery(id+"F0.wireOp",EDGE,"E24")])]});
            transform(context, id + "F24", {"entities" : qUnion([Q0]), "transformType" : TransformType.TRANSLATION_3D, "dx" : 0 * mm, "dy" : 0 * mm, "dz" : 2.1 * mm, "makeCopy" : false});
        }
        {
            var Q0;
            Q0=makeQuery(id+"F5.opExtrude","SWEPT_BODY",BODY,{"disambiguationData":[OSD([sQuery(id+"F0.wireOp",EDGE,"E2.4"),sQuery(id+"F0.wireOp",EDGE,"E2.5"),sQuery(id+"F0.wireOp",EDGE,"E4"),sQuery(id+"F0.wireOp",EDGE,"E6"),sQuery(id+"F0.wireOp",EDGE,"E9.0"),sQuery(id+"F0.wireOp",EDGE,"E11.0"),sQuery(id+"F0.wireOp",EDGE,"E26"),sQuery(id+"F0.wireOp",EDGE,"E27")])]});
            transform(context, id + "F25", {"entities" : qUnion([Q0]), "transformType" : TransformType.TRANSLATION_3D, "dx" : 0 * mm, "dy" : 0 * mm, "dz" : -0.5 * mm, "makeCopy" : false});
        }
    });
